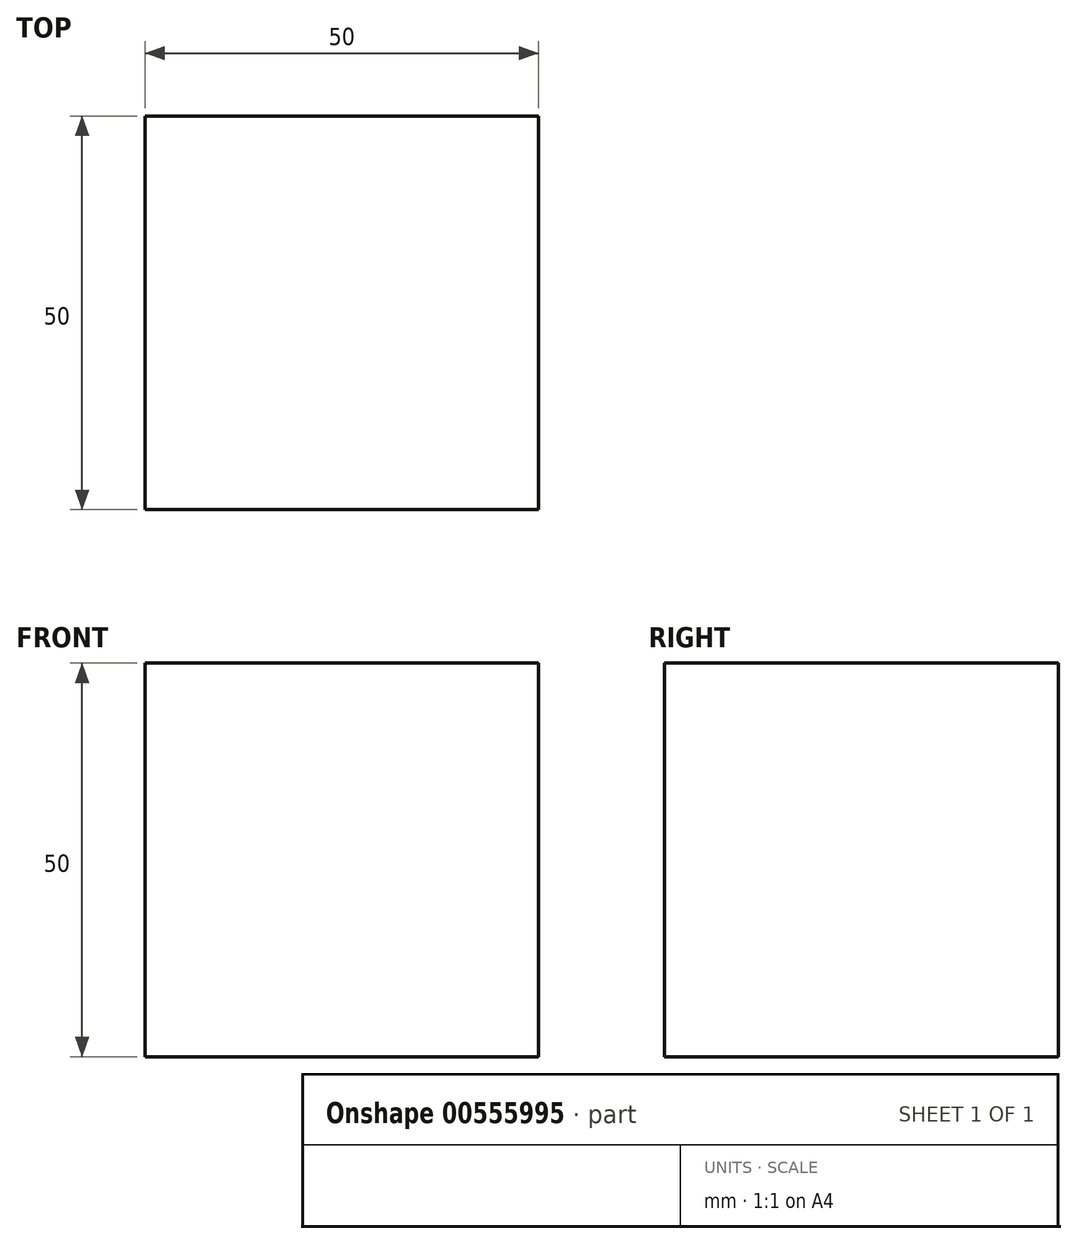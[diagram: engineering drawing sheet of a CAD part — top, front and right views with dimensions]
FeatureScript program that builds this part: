
annotation { "Feature Type Name" : "Feature", "Feature Type Description" : "" }
export const myFeature = defineFeature(function(context is Context, id is Id, definition is map)
    precondition{}
    {
        {
            var Q0;
            Q0=qCreatedBy(makeId("Top.planeOp"),FACE);
            var sketch = newSketch(context, id + "F0", { "sketchPlane" : qUnion([Q0])});
            skLineSegment(sketch, "E0.bottom", {"start": v(-15, 27.17) * mm, "end": v(35, 27.17) * mm});
            skLineSegment(sketch, "E0.top", {"start": v(-15, -22.83) * mm, "end": v(35, -22.83) * mm});
            skLineSegment(sketch, "E0.left", {"start": v(-15, 27.17) * mm, "end": v(-15, -22.83) * mm});
            skLineSegment(sketch, "E0.right", {"start": v(35, 27.17) * mm, "end": v(35, -22.83) * mm});
            skSolve(sketch);
        }
        {
            var Q0;
            Q0=makeQuery(id+"F0.imprint","IMPRINT",FACE,{"disambiguationData":[TD([[makeQuery(id+"F0.imprint","IMPRINT",EDGE,{"derivedFrom":sQuery(id+"F0.wireOp",EDGE,"E0.bottom")}),-1.0]])]});
            extrude(context, id + "F1", {"entities" : qUnion([Q0]), "depth" : 50 * mm, "offsetDistance" : 25 * mm});
        }
    });
